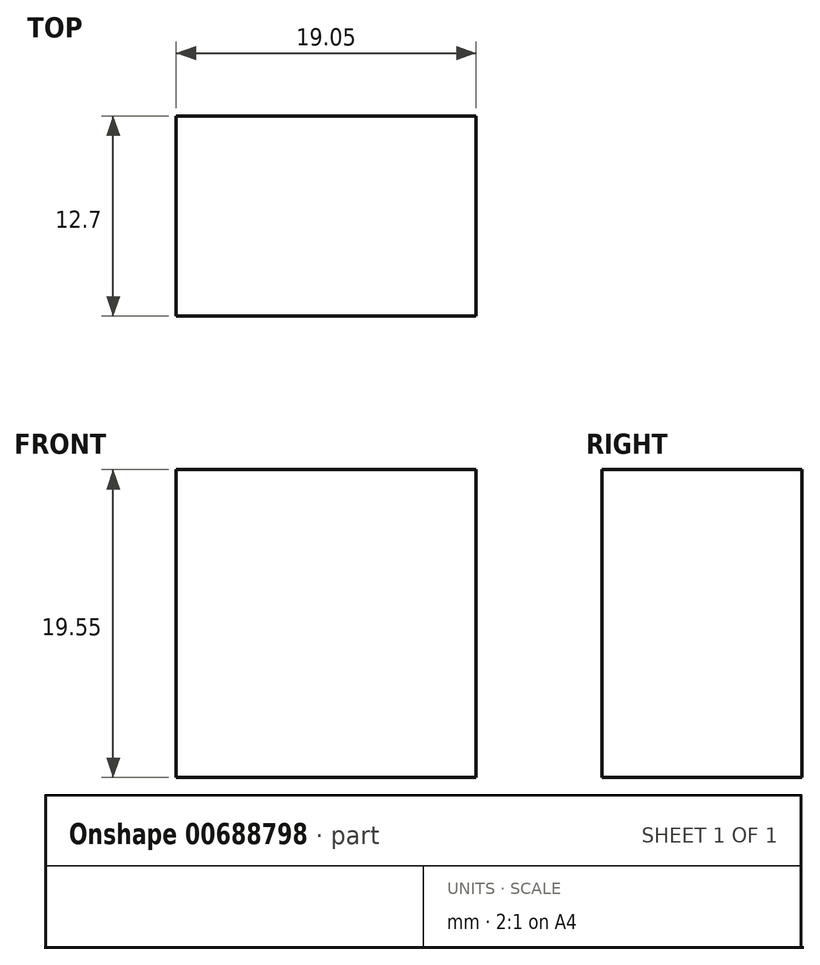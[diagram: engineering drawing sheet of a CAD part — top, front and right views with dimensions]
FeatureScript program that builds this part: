
annotation { "Feature Type Name" : "Feature", "Feature Type Description" : "" }
export const myFeature = defineFeature(function(context is Context, id is Id, definition is map)
    precondition{}
    {
        {
            var Q0;
            Q0=qCreatedBy(makeId("Front.planeOp"),FACE);
            var sketch = newSketch(context, id + "F0", { "sketchPlane" : qUnion([Q0])});
            skLineSegment(sketch, "E0", {"start": v(0, 19.55) * mm, "end": v(-19.05, 19.55) * mm});
            skLineSegment(sketch, "E1", {"start": v(-19.05, 19.55) * mm, "end": v(-19.05, 0) * mm});
            skLineSegment(sketch, "E2", {"start": v(-19.05, 0) * mm, "end": v(0, 0) * mm});
            skLineSegment(sketch, "E3", {"start": v(0, 0) * mm, "end": v(0, 19.55) * mm});
            skSolve(sketch);
        }
        {
            var Q0;
            Q0 = qSketchRegion(id + "F0", true);
            extrude(context, id + "F1", {"entities" : qUnion([Q0]), "depth" : 12.7 * mm, "offsetDistance" : 25.4 * mm});
        }
    });
